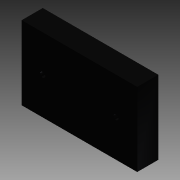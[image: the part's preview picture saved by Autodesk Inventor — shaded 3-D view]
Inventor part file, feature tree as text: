
AUTODESK INVENTOR PART (.ipt)
format: ipt  version: 2015 (Build 190159000, 159)  size: 81,920 bytes
history: native  units: mm
features: hole x2, extrude x1, sketch x1
ambient origin geometry x8: Origin, YZ Plane, XZ Plane, XY Plane, X Axis, Y Axis, Z Axis, Center Point
bodies: Volumenkörper1 (feature_tree)
feature tree (4):
  extrude  "Extrusion1"  Depth=57.5mm
  hole  "Bohrung1"  [1 undecoded]
  hole  "Bohrung2"  [1 undecoded]
  sketch  "Skizze1"  dims[d0=90.25mm d1=57.5mm d2=16.5mm d3=0.0mm d4=16.5mm d5=28.75mm d6=4.0mm d7=6.0mm d8=4.0mm d9=2.0mm d10=90.0deg d11=8.0mm d12=20.594885mm d13=28.75mm d14=16.5mm d15=4.0mm d16=6.0mm d17=4.0mm d18=2.0mm d19=90.0deg d20=8.0mm d21=20.594885mm]
note: 2 required parameter values undecoded (feature->parameter linkage not recoverable at this tier; creation-order binding heuristic only, values carry confidence <= 0.55)
